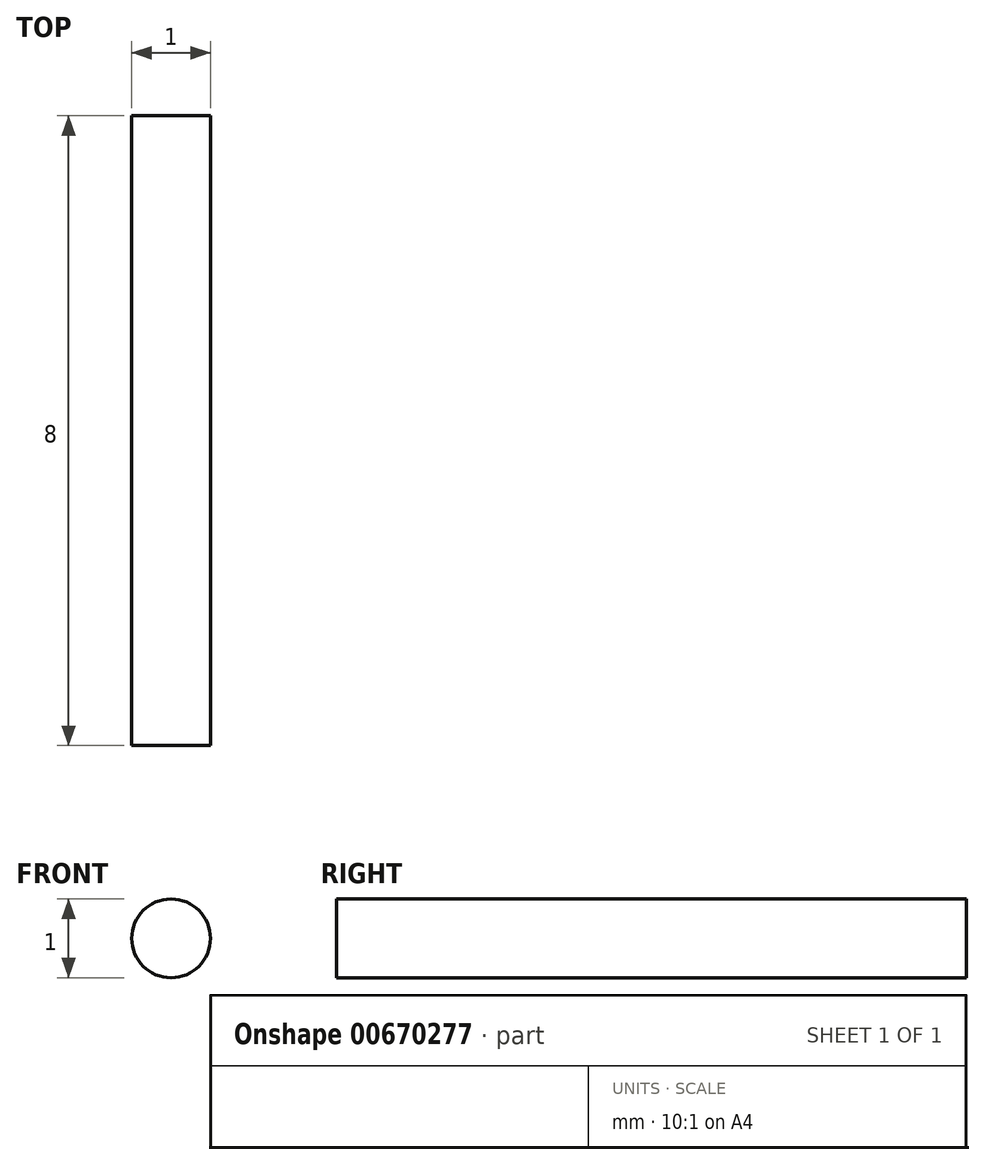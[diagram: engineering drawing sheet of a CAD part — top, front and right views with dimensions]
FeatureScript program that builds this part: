
annotation { "Feature Type Name" : "Feature", "Feature Type Description" : "" }
export const myFeature = defineFeature(function(context is Context, id is Id, definition is map)
    precondition{}
    {
        {
            var Q0;
            Q0=qCreatedBy(makeId("Front.planeOp"),FACE);
            var sketch = newSketch(context, id + "F0", { "sketchPlane" : qUnion([Q0])});
            skCircle(sketch, "E0", {"center": v(0, 0) * mm, "radius": 0.5 * mm});
            skSolve(sketch);
        }
        {
            var Q0;
            Q0=makeQuery(id+"F0.imprint","IMPRINT",FACE,{"disambiguationData":[TD([[makeQuery(id+"F0.imprint","IMPRINT",EDGE,{"derivedFrom":sQuery(id+"F0.wireOp",EDGE,"E0")}),1.0]])]});
            extrude(context, id + "F1", {"entities" : qUnion([Q0]), "depth" : 4 * mm, "offsetDistance" : 25 * mm, "hasSecondDirection" : true, "secondDirectionOppositeDirection" : true, "secondDirectionDepth" : 4 * mm});
        }
    });
